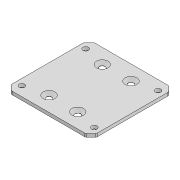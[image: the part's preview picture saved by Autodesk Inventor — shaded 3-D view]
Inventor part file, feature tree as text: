
AUTODESK INVENTOR PART (.ipt)
format: ipt  version: 2020 (Build 240168000, 168)  size: 126,976 bytes
history: native  units: mm
features: sketch x3, hole x2, other x1, extrude x1, chamfer x1, fillet x1
ambient origin geometry x8: Origin, YZ Plane, XZ Plane, XY Plane, X Axis, Y Axis, Z Axis, Center Point
bodies: Body1 (feature_tree)
feature tree (9):
  other  "ソリッド1"
  extrude  "押し出し1"  Depth=80.0mm
  hole  "穴1"  [1 undecoded]
  hole  "穴2"  [1 undecoded]
  chamfer  "面取り1"  Distance=68.0mm
  fillet  "フィレット3"  Radius=60.0mm
  sketch  "スケッチ1"
  sketch  "スケッチ2"
  sketch  "スケッチ3"
note: 2 required parameter values undecoded (feature->parameter linkage not recoverable at this tier; creation-order binding heuristic only, values carry confidence <= 0.55)
